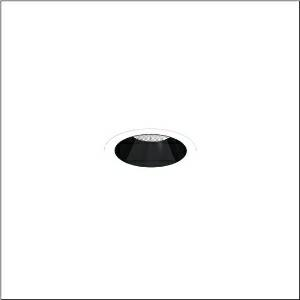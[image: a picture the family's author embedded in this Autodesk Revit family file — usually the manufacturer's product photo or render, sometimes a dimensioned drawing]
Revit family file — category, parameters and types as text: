
# Revit family: lunis_21_m_51db17ec91c
name_source: partatom
category: Lighting Fixtures
units: mm (PartAtom-declared; Revit-internal decimal feet)

## family parameters
Cut with Voids When Loaded = No
Host = Face
Light Source = No
Part Type = Normal
Room Calculation Point = No
Round Connector Dimension = Use Diameter
Shared = No

## types (1)
- --- (1 x LED, 3310 lm, 25.5 W, 6500K)
    Apparent Load = 26 VA
    CIE Flux Codes = 98 100 100 100 100
    Color Rendering = 80
    Color Temperature = 6500K
    Default Elevation = 1800 mm
    Description = Lunis 21 M, downlight, light control with lens, of PMMA, anti glare with reflector, of PC, light emission: direct distribution, LED rated luminous flux: 1.540lm, light colour: 830/840/865, with terminal, 5-pole, mains connection: 220..240V, AC/DC, 0/50..60Hz, housing, round, of diecast aluminium, traffic white (RAL 9016), diameter: 115mm, clamping range: 1..40mm, protection rating (complete): IP20, protection rating (on room side): IP54, insulation class (complete): insulation class II (safety insulation), certification: CE, impact resistance: IK03, packaging unit: 1 piece
    Height = 0 mm  [stored 0 ft]
    Lamp = 1 x LED
    Lamp Light Flux = 3310 lm
    Lamp Power = 25.5 W
    Lamp count = 1
    Length = 115 mm
    Luminous efficacy = 130 lm/W
    Manufacturer = Siteco
    ModVariant = No
    Model = 51DB17EC91C
    Mounting Place = Ceiling
    Mounting Type = Recessed
    Number of Poles = 1
    OnlyDefault = Yes
    Power Factor = 1
    Product Name = Lunis 21 M
    Product group = downlight
    ProductGroupID = 401
    Protection Class = Protection class II
    Protection Degree = IP 20
    RLX_Detail_Level = 1
    RLX_Emergency_Light_Flux = 0 lm
    RLX_Emergency_Type = 0
    RLX_Emergency_Type_DB = No
    RlxData = <blob elided: 14937 chars, md5=94062c63>
    Socket = socket
    Standby Power = 0 W
    System Light Flux = 3310 lm
    System Power = 26 W
    Type Comments = individual setting: colour temperature 6500K, luminous flux: 100 % | (ON | ON | OFF | OFF) | 700 mA
    Type Image = l_1290854.jpg
    URL = http://relux.com
    VarID = @adj_035909
    Voltage = 0 V
    Weight = 0.00 kg
    Width = 0 mm  [stored 0 ft]

note: [stored X ft] marks values corroborated as IEEE doubles in the binary element streams (Revit-internal decimal feet)

## geometry (parser evidence)
native form markers: Sweep x10
no freeform markers — native parametric forms only
